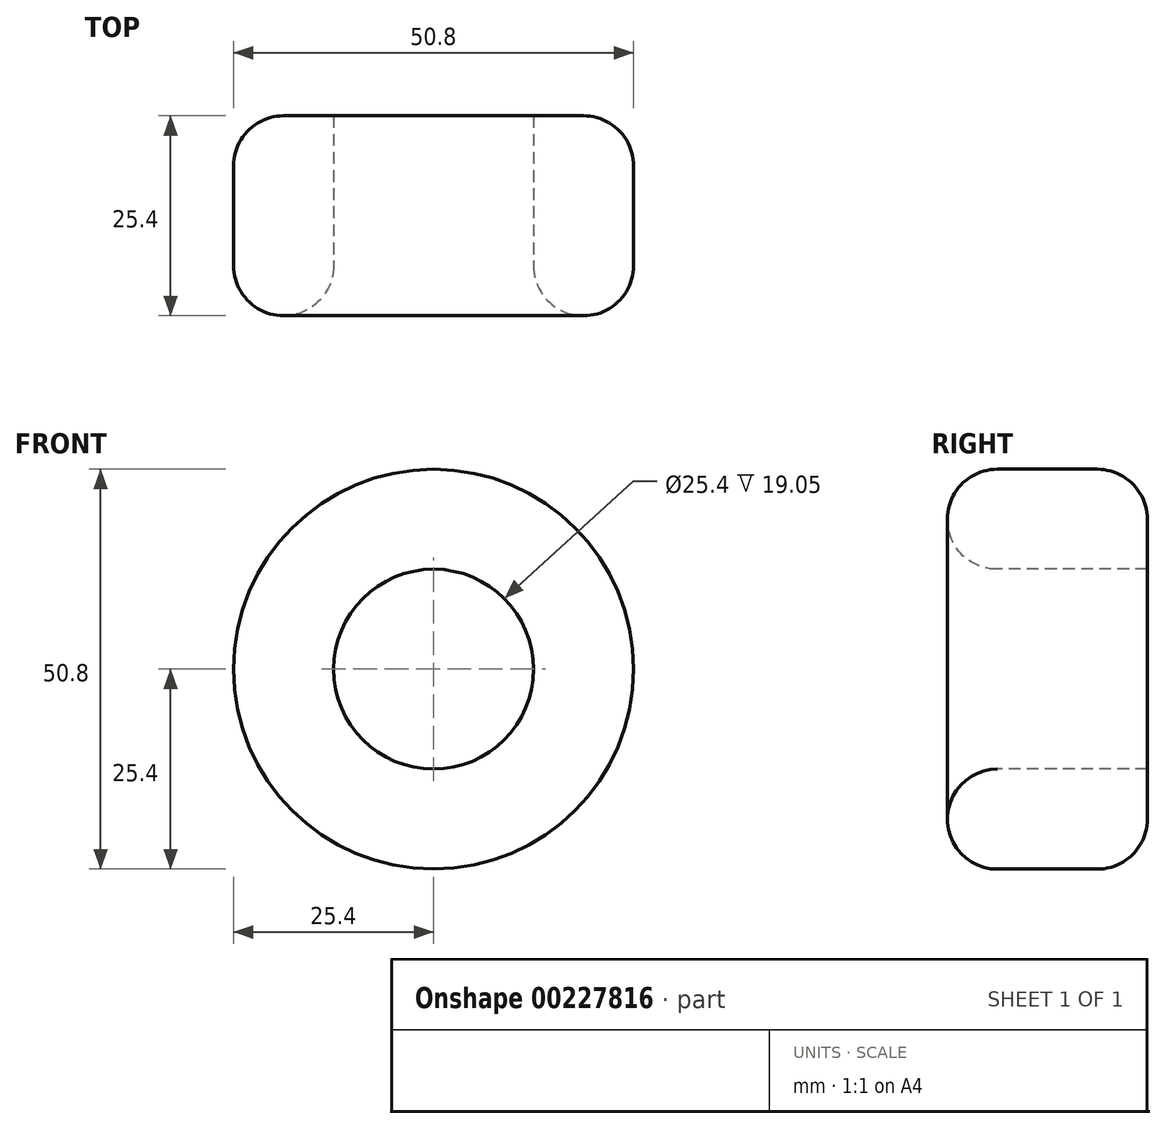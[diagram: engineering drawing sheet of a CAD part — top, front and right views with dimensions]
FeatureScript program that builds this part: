
annotation { "Feature Type Name" : "Feature", "Feature Type Description" : "" }
export const myFeature = defineFeature(function(context is Context, id is Id, definition is map)
    precondition{}
    {
        {
            var Q0;
            Q0=qCreatedBy(makeId("Top.planeOp"),FACE);
            var sketch = newSketch(context, id + "F0", { "sketchPlane" : qUnion([Q0])});
            skCircle(sketch, "E0", {"center": v(0, 0) * mm, "radius": 17.02 * mm});
            skSolve(sketch);
        }
        {
            var Q0;
            Q0=sQuery(id+"F0.wireOp",EDGE,"E0");
            extrude(context, id + "F1", {"bodyType" : ToolBodyType.SURFACE, "surfaceEntities" : qUnion([Q0]), "depth" : 25.4 * mm});
        }
        {
            var Q0;
            Q0=makeQuery(id+"F1.opExtrude","SWEPT_BODY",BODY,{"disambiguationData":[OSD([sQuery(id+"F0.wireOp",EDGE,"E0")])]});
            deleteBodies(context, id + "F2", {"entities" : qUnion([Q0])});
        }
        {
            var Q0;
            Q0=qCreatedBy(makeId("Front.planeOp"),FACE);
            var sketch = newSketch(context, id + "F3", { "sketchPlane" : qUnion([Q0])});
            skCircle(sketch, "E1", {"center": v(0, 0) * mm, "radius": 25.4 * mm});
            skSolve(sketch);
        }
        {
            var Q0;
            Q0=makeQuery(id+"F3.imprint","IMPRINT",FACE,{"disambiguationData":[TD([[makeQuery(id+"F3.imprint","IMPRINT",EDGE,{"derivedFrom":sQuery(id+"F3.wireOp",EDGE,"E1")}),1.0]])]});
            extrude(context, id + "F4", {"entities" : qUnion([Q0]), "depth" : 25.4 * mm});
        }
        {
            var Q0;
            Q0=makeQuery(id+"F4.opExtrude","CAP_FACE",FACE,{"disambiguationData":[OSD([sQuery(id+"F3.wireOp",EDGE,"E1")])],"isStart":false});
            var sketch = newSketch(context, id + "F5", { "sketchPlane" : qUnion([Q0])});
            skCircle(sketch, "E2", {"center": v(0, 0) * mm, "radius": 12.7 * mm});
            skSolve(sketch);
        }
        {
            var Q0;
            Q0=sQuery(id+"F5.wireOp",VERTEX,"E2.center");
            var Q1;
            Q1=makeQuery(id+"F4.opExtrude","SWEPT_BODY",BODY,{"disambiguationData":[OSD([sQuery(id+"F3.wireOp",EDGE,"E1")])]});
            hole(context, id + "F6", {"style" : HoleStyle.SIMPLE, "endStyle" : HoleEndStyle.THROUGH, "holeDiameter" : 25.4 * mm, "locations" : qUnion([Q0]), "scope" : qUnion([Q1]), "isTappedThrough" : true});
        }
        {
            var Q0;
            Q0=makeQuery(id+"F4.opExtrude","CAP_FACE",FACE,{"disambiguationData":[OSD([sQuery(id+"F3.wireOp",EDGE,"E1")])],"isStart":false});
            fillet(context, id + "F7", {"entities" : qUnion([Q0]), "radius" : 6.35 * mm, "tangentPropagation" : true, "allowEdgeOverflow" : false});
        }
        {
            var Q0;
            Q0=makeQuery(id+"F4.opExtrude","CAP_EDGE",EDGE,{"disambiguationData":[OSD([sQuery(id+"F3.wireOp",EDGE,"E1")])],"isStart":true});
            fillet(context, id + "F8", {"entities" : qUnion([Q0]), "radius" : 6.35 * mm, "tangentPropagation" : true, "allowEdgeOverflow" : false});
        }
    });
